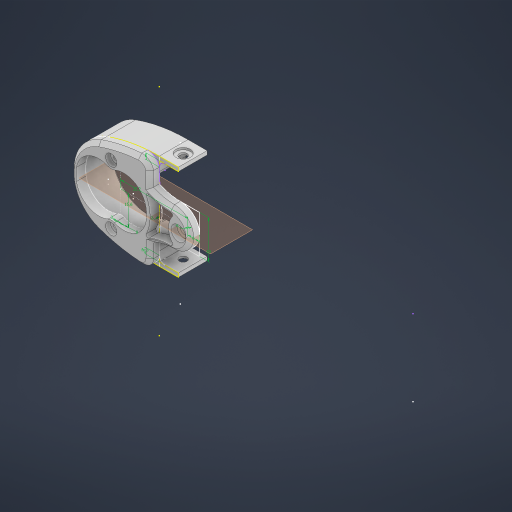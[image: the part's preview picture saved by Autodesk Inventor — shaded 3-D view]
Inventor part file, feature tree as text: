
AUTODESK INVENTOR PART (.ipt)
format: ipt  version: 2024.2 (Build 282272000, 272)  size: 729,088 bytes
history: native  units: in
note: dims shown in document units (in); Inventor stores cm internally (conversion verified against a paired STEP export)
features: extrude x8, sketch x8, projected_geometry x5, mirror x2, chamfer x2, plane x1, fillet x1
ambient origin geometry x8: Origin, YZ Plane, XZ Plane, XY Plane, X Axis, Y Axis, Z Axis, Center Point
bodies: Solid1 (feature_tree)
feature tree (27):
  extrude  "Extrusion1"  Depth=1.9685in
  plane  "Work Plane1"
  sketch  "Sketch2"  dims[d3=0.0787in d4=1.6929in]
  extrude  "Extrusion2"  Depth=0.0787in
  extrude  "Extrusion4"  Depth=0.1181in
  mirror  "Mirror2"
  extrude  "Extrusion5"  Depth=0.315in
  extrude  "Extrusion7"  Depth=1.3858in
  extrude  "Extrusion8"  Depth=0.7874in
  mirror  "Mirror4"
  chamfer  "Chamfer1"  Distance=0.1969in
  extrude  "Extrusion11"  Depth=0.0984in TaperAngle=0.0deg
  fillet  "Fillet3"  Radius=0.1181in
  chamfer  "Chamfer4"  Distance=0.1181in
  extrude  "Extrusion12"  Depth=0.0787in
  sketch  "Sketch1"  dims[d0=1.4567in d2=1.9685in]
  projected_geometry  "Projected Loop1"
  sketch  "Sketch3"  dims[d6=0.5906in d7=0.0in d8=0.1181in]
  projected_geometry  "Projected Loop2"
  sketch  "Sketch4"  dims[d9=0.6142in d10=0.315in]
  projected_geometry  "Projected Loop3"
  sketch  "Sketch5"  dims[d11=0.0787in d12=1.3858in]
  projected_geometry  "Projected Loop4"
  sketch  "Sketch6"  dims[d13=0.1575in d14=0.7874in]
  projected_geometry  "Projected Loop5"
  sketch  "Sketch9"  dims[d15=0.2362in d16=0.1969in d17=0.0in]
  sketch  "Sketch10"  dims[d20=0.2323in d21=0.0984in d22=0.0in d23=0.1181in d24=0.1181in d25=0.0787in d26=0.1575in d28=0.3937in d30=0.7087in d32=0.1969in d33=0.0in d36=0.1575in d37=0.1969in d38=0.0in d39=0.0in d40=0.2953in d41=0.0394in d42=0.0in d45=0.0787in d46=0.0787in d47=45.0deg d52=0.7953in d53=0.3937in d62=0.2756in d63=0.8661in d64=0.3937in d65=0.0in d66=0.0787in d67=0.0394in d68=0.0787in d69=45.0deg d70=0.3031in d71=0.1181in d72=0.0in d54=0.0197in d55=0.0344in d56=0.0197in d57=0.0344in]
